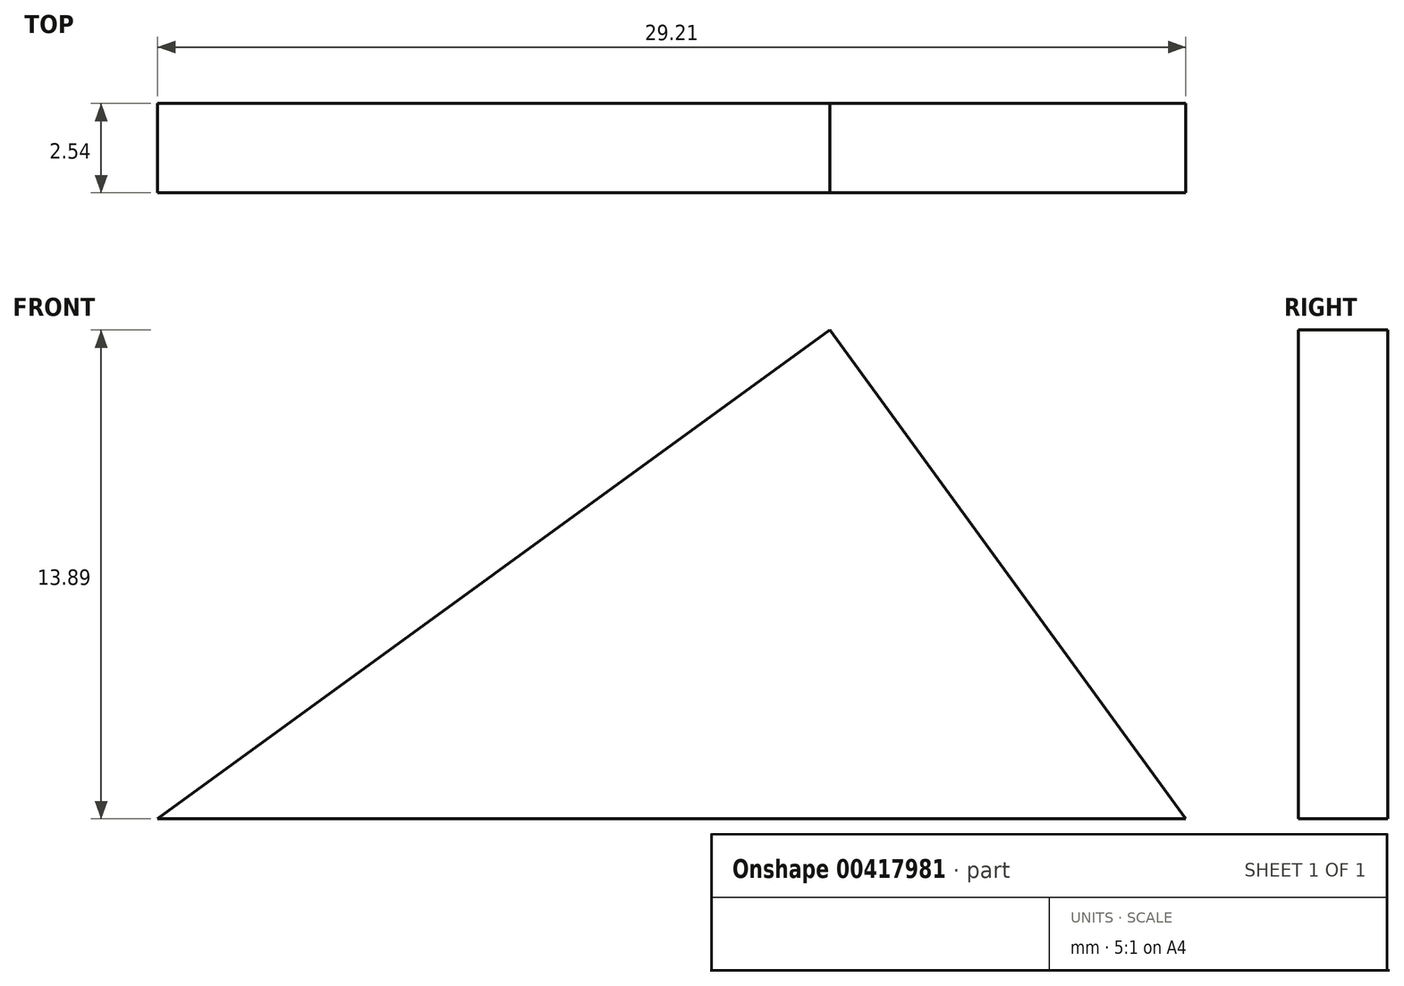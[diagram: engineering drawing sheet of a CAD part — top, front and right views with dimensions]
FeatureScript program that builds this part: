
annotation { "Feature Type Name" : "Feature", "Feature Type Description" : "" }
export const myFeature = defineFeature(function(context is Context, id is Id, definition is map)
    precondition{}
    {
        {
            var Q0;
            Q0=qCreatedBy(makeId("Front.planeOp"),FACE);
            var sketch = newSketch(context, id + "F0", { "sketchPlane" : qUnion([Q0])});
            skLineSegment(sketch, "E0", {"start": v(27.42, 25.8) * mm, "end": v(27.42, 25.8) * mm});
            skLineSegment(sketch, "E1", {"start": v(27.42, 25.8) * mm, "end": v(46.52, 39.7) * mm});
            skLineSegment(sketch, "E2", {"start": v(46.52, 39.7) * mm, "end": v(56.63, 25.8) * mm});
            skLineSegment(sketch, "E3", {"start": v(56.63, 25.8) * mm, "end": v(27.42, 25.8) * mm});
            skSolve(sketch);
        }
        {
            var Q0;
            Q0=makeQuery(id+"F0.imprint","IMPRINT",FACE,{"disambiguationData":[TD([[makeQuery(id+"F0.imprint","IMPRINT",EDGE,{"derivedFrom":sQuery(id+"F0.wireOp",EDGE,"E1")}),-1.0]])]});
            extrude(context, id + "F1", {"entities" : qUnion([Q0]), "depth" : 2.54 * mm});
        }
    });
